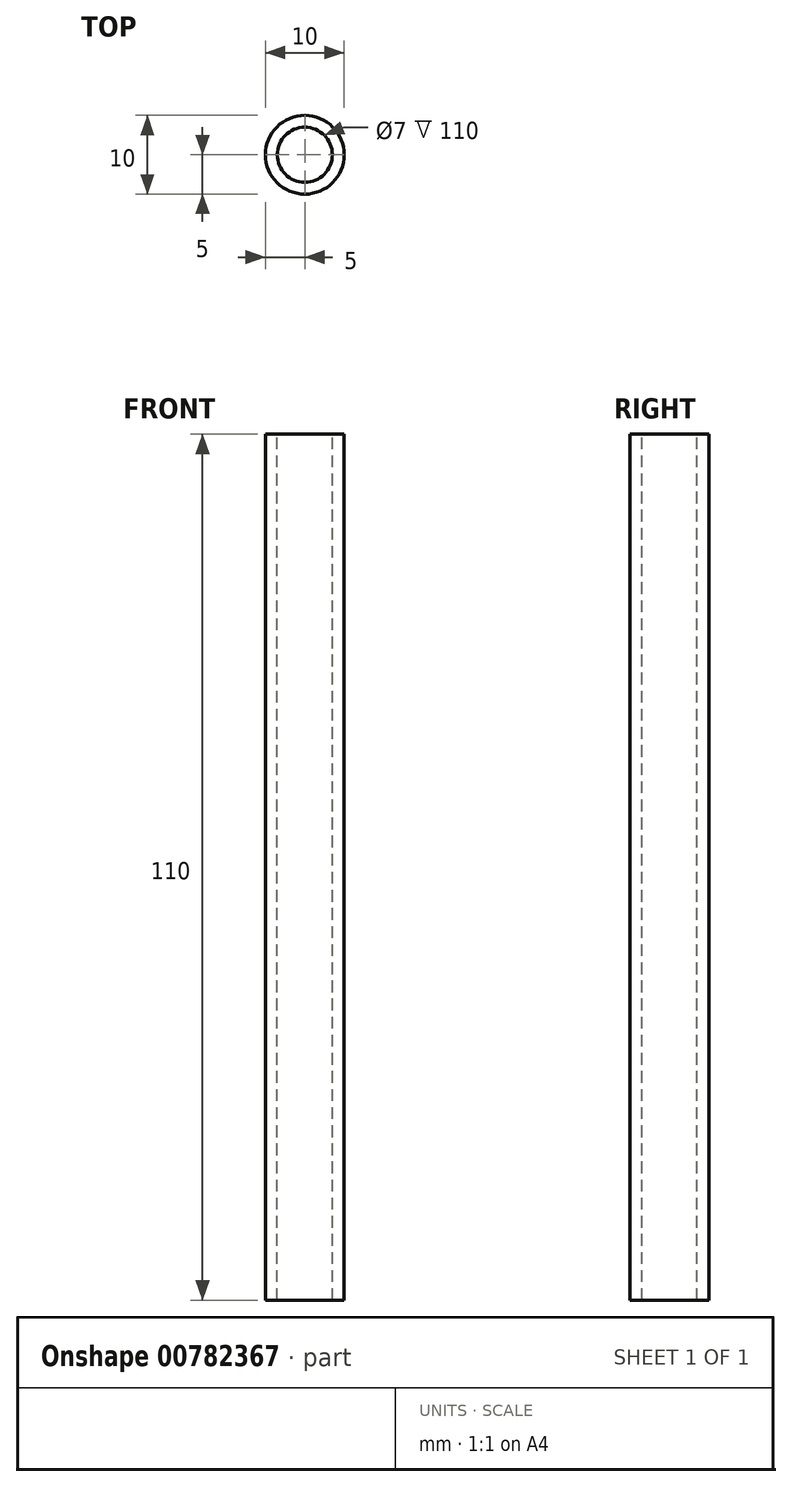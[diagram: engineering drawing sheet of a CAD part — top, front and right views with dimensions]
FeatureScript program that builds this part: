
annotation { "Feature Type Name" : "Feature", "Feature Type Description" : "" }
export const myFeature = defineFeature(function(context is Context, id is Id, definition is map)
    precondition{}
    {
        {
            var Q0;
            Q0=qCreatedBy(makeId("Front.planeOp"),FACE);
            var sketch = newSketch(context, id + "F0", { "sketchPlane" : qUnion([Q0])});
            skLineSegment(sketch, "E0", {"start": v(-5, 0) * mm, "end": v(-5, 55) * mm});
            skLineSegment(sketch, "E1", {"start": v(-5, 55) * mm, "end": v(0, 55) * mm});
            skLineSegment(sketch, "E2.MirrorCS", {"start": v(-5, 0) * mm, "end": v(-5, -55) * mm});
            skLineSegment(sketch, "E3.MirrorCS", {"start": v(-5, -55) * mm, "end": v(0, -55) * mm});
            skLineSegment(sketch, "E4", {"start": v(0, 55) * mm, "end": v(0, -55) * mm});
            skSolve(sketch);
        }
        {
            var Q0;
            Q0 = qSketchRegion(id + "F0", true);
            var Q1;
            Q1=sQuery(id+"F0.wireOp",EDGE,"E4");
            revolve(context, id + "F1", {"surfaceOperationType" : NewSurfaceOperationType.NEW, "entities" : qUnion([Q0]), "axis" : qUnion([Q1]), "revolveType" : RevolveType.FULL});
        }
        {
            var Q0;
            Q0=makeQuery(id+"F1.opRevolve","SWEPT_FACE",FACE,{"disambiguationData":[OSD([sQuery(id+"F0.wireOp",EDGE,"E1")])]});
            var Q1;
            Q1=makeQuery(id+"F1.opRevolve","SWEPT_FACE",FACE,{"disambiguationData":[OSD([sQuery(id+"F0.wireOp",EDGE,"E3.MirrorCS")])]});
            var Q2;
            Q2=makeQuery(id+"F1.opRevolve","SWEPT_BODY",BODY,{"disambiguationData":[OSD([sQuery(id+"F0.wireOp",EDGE,"E0"),sQuery(id+"F0.wireOp",EDGE,"E1"),sQuery(id+"F0.wireOp",EDGE,"E2.MirrorCS"),sQuery(id+"F0.wireOp",EDGE,"E3.MirrorCS"),sQuery(id+"F0.wireOp",EDGE,"E4")])]});
            shell(context, id + "F2", {"entities" : qUnion([Q0, Q1]), "parts" : qUnion([Q2]), "thickness" : 1.5 * mm});
        }
    });
